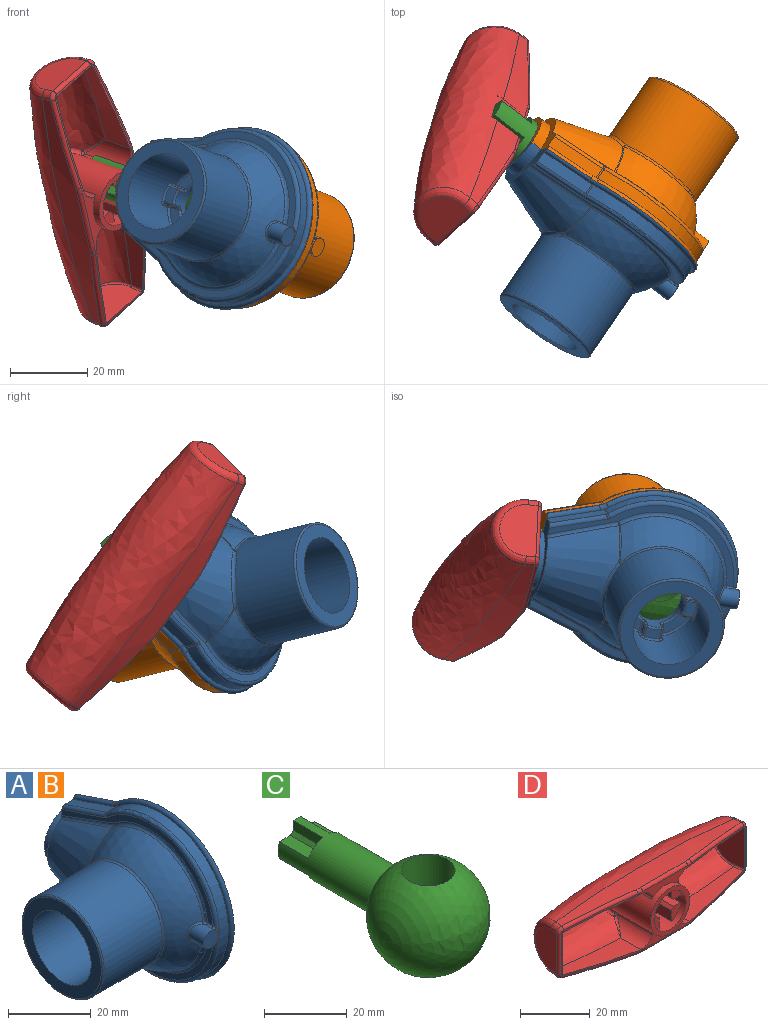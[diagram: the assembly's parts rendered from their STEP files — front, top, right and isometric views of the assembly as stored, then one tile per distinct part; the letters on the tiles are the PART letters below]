
ASSEMBLY  parts=4 mates=3
PART A: 151 faces, bbox 35.9x59.5x52.1 mm
  f0: plane 1.96x1.09mm, normal (-1,0,0), area 0.1mm2, adj f1,f148,f149,f150
  f1: cylinder r=1mm len=3mm, axis (1,0,0), area 1.2mm2, adj f0,f2,f148,f150
  f2: torus R=2mm, axis (1,0,0), area 0.9mm2, adj f1,f3,f146,f147
  f3: torus R=22mm, axis (1,0,0), area 158.3mm2, adj f2,f4,f142,f143,f144,f145,f147,f148
  f4: torus R=2mm, axis (1,0,0), area 0.9mm2, adj f3,f5,f141,f145
  f5: cylinder r=1mm len=3mm, axis (1,0,0), area 1.2mm2, adj f4,f6,f140,f148
  f6: plane 1.96x1.09mm, normal (-1,0,0), area 0.1mm2, adj f5,f7,f140,f148
  f7: torus R=6mm, axis (1,0,0), area 3.2mm2, adj f6,f8,f138,f139
  f8: plane 57x48mm, normal (1,0,0), area 1146.2mm2, adj f7,f9,f133,f134,f135,f136,f137,f138
  f9: sphere r=15mm, area 1204.3mm2, adj f8,f10,f133
  f10: cylinder r=6.5mm len=13mm, axis (-1,0,0), area 127.8mm2, adj f9,f11,f110,f111,f112,f113,f114,f115
  f11: cylinder r=0.5mm len=2mm, axis (-1,0,0), area 1.9mm2, adj f10,f12,f109,f132
  f12: sphere r=0.5mm, area 0.5mm2, adj f11,f13,f110
  f13: cylinder r=0.5mm len=2.58mm, axis (0,0,-1), area 1.9mm2, adj f12,f14,f108,f109
  f14: plane 4x2.79mm, normal (-1,0,0), area 10.1mm2, adj f13,f15,f107,f110
  f15: cylinder r=0.5mm len=2.58mm, axis (0,0,1), area 1.9mm2, adj f14,f16,f17,f106
  f16: sphere r=0.5mm, area 0.5mm2, adj f15,f110,f111
  f17: plane 2.31x2mm, normal (0,1,0), area 4.6mm2, adj f15,f18,f105,f111
  f18: cylinder r=0.5mm len=2.69mm, axis (0,0,-1), area 2mm2, adj f17,f19,f104,f112
  f19: sphere r=0.5mm, area 0.5mm2, adj f18,f20,f105
  f20: torus R=9.5mm, axis (-1,0,0), area 7.2mm2, adj f19,f21,f103,f104
  f21: cylinder r=10mm len=20mm, axis (-1,0,0), area 1089.6mm2, adj f20,f22,f61,f85,f86,f87,f88,f89
  f22: cylinder r=0.5mm len=2mm, axis (-1,0,0), area 1.9mm2, adj f21,f23,f102,f103
  f23: plane 2.31x2mm, normal (0,0,1), area 4.6mm2, adj f22,f24,f60,f115
  f24: cylinder r=0.5mm len=2.58mm, axis (0,-1,0), area 1.9mm2, adj f23,f25,f26,f102
  f25: sphere r=0.5mm, area 0.3mm2, adj f24,f115,f116
  f26: plane 4x2.79mm, normal (-1,0,0), area 10.1mm2, adj f24,f27,f101,f116
  f27: cylinder r=0.5mm len=2.58mm, axis (0,1,0), area 1.9mm2, adj f26,f28,f29,f100
  f28: sphere r=0.5mm, area 0.4mm2, adj f27,f116,f117
  f29: plane 2.31x2mm, normal (0,0,-1), area 4.6mm2, adj f27,f30,f99,f117
  f30: cylinder r=0.5mm len=2.69mm, axis (0,-1,0), area 2mm2, adj f29,f31,f32,f118
  f31: sphere r=0.5mm, area 0.7mm2, adj f30,f98,f99
  f32: plane 6.01x6.01mm, normal (-1,0,0), area 17mm2, adj f30,f33,f98,f119
  f33: cylinder r=0.5mm len=2.69mm, axis (0,0,-1), area 2mm2, adj f32,f34,f35,f120
  f34: sphere r=0.5mm, area 0.5mm2, adj f33,f97,f98
  f35: plane 2.31x2mm, normal (0,1,0), area 4.6mm2, adj f33,f36,f97,f121
  f36: cylinder r=0.5mm len=2.58mm, axis (0,0,1), area 1.9mm2, adj f35,f37,f38,f96
  f37: sphere r=0.5mm, area 0.5mm2, adj f36,f121,f122
  f38: plane 4x2.79mm, normal (-1,0,0), area 10.1mm2, adj f36,f39,f95,f122
  f39: cylinder r=0.5mm len=2.58mm, axis (0,0,-1), area 1.9mm2, adj f38,f40,f41,f94
  f40: sphere r=0.5mm, area 0.5mm2, adj f39,f122,f123
  f41: plane 2.31x2mm, normal (0,-1,0), area 4.6mm2, adj f39,f42,f93,f123
  f42: cylinder r=0.5mm len=2.69mm, axis (0,0,1), area 2mm2, adj f41,f43,f44,f124
  f43: sphere r=0.5mm, area 0.5mm2, adj f42,f92,f93
  f44: plane 6.01x6.01mm, normal (-1,0,0), area 17mm2, adj f42,f45,f92,f125
  f45: cylinder r=0.5mm len=2.69mm, axis (0,-1,0), area 2mm2, adj f44,f46,f47,f126
  f46: sphere r=0.5mm, area 0.6mm2, adj f45,f91,f92
  f47: plane 2.31x2mm, normal (0,0,-1), area 4.6mm2, adj f45,f48,f91,f127
  f48: cylinder r=0.5mm len=2.58mm, axis (0,1,0), area 1.9mm2, adj f47,f49,f50,f90
  f49: sphere r=0.5mm, area 0.8mm2, adj f48,f127,f128
  f50: plane 4x2.79mm, normal (-1,0,0), area 10.1mm2, adj f48,f51,f89,f128
  f51: cylinder r=0.5mm len=2.58mm, axis (0,-1,0), area 1.9mm2, adj f50,f52,f53,f54,f88
  f52: sphere r=0.5mm, area 0mm2, adj f51,f129
  f53: sphere r=0.5mm, area 0.2mm2, adj f51,f128,f129
  f54: plane 2.31x2mm, normal (0,0,1), area 4.6mm2, adj f51,f55,f87,f129
  f55: cylinder r=0.5mm len=2.69mm, axis (0,1,0), area 2mm2, adj f54,f56,f57,f130
  f56: sphere r=0.5mm, area 0.6mm2, adj f55,f86,f87
  f57: plane 6.01x6.01mm, normal (-1,0,0), area 17mm2, adj f55,f58,f86,f131
  f58: cylinder r=0.5mm len=2.69mm, axis (0,0,1), area 2mm2, adj f57,f59,f109,f132
  f59: sphere r=0.5mm, area 0.5mm2, adj f58,f85,f86
  f60: cylinder r=0.5mm len=2.69mm, axis (0,1,0), area 2mm2, adj f23,f103,f104,f114
  f61: plane 27x27mm, normal (-1,0,0), area 258.4mm2, adj f21,f62
  f62: torus R=13.5mm, axis (1,0,0), area 68.2mm2, adj f61,f63
  f63: cylinder r=14mm len=28mm, axis (1,0,0), area 1742mm2, adj f62,f64,f84
  f64: bspline ~17.52x3.73mm, area 19.6mm2, adj f63,f65,f82,f83
  f65: sphere r=1mm, area 0.1mm2, adj f64,f66,f84
  f66: torus R=16.9mm, axis (0,-1,0), area 3.5mm2, adj f65,f67,f81,f82
  f67: sphere r=1mm, area 0.1mm2, adj f66,f68,f69
  f68: bspline ~23.13x9.23mm, area 21.5mm2, adj f67,f82,f136,f145
  f69: torus R=20.12mm, axis (1,0,0), area 52.7mm2, adj f67,f70,f81,f145
  f70: bspline ~1.33x1.14mm, area 1mm2, adj f69,f71,f72,f79
  f71: cylinder r=0.5mm len=1.89mm, axis (0,1,0), area 2mm2, adj f70,f79,f144,f145
  f72: bspline ~5.86x4.64mm, area 6.9mm2, adj f70,f73,f79,f81
  f73: bspline ~1.33x1.14mm, area 1mm2, adj f72,f74,f75,f79
  f74: cylinder r=0.5mm len=1.89mm, axis (0,1,0), area 2mm2, adj f73,f79,f142,f147
  f75: torus R=20.12mm, axis (1,0,0), area 52.7mm2, adj f73,f76,f81,f147
  f76: sphere r=1mm, area 0.2mm2, adj f75,f77,f78
  f77: torus R=16.9mm, axis (0,-1,0), area 3.5mm2, adj f76,f81,f82,f83
  f78: bspline ~25.11x10.02mm, area 21.5mm2, adj f76,f82,f136,f147
  f79: cylinder r=2.5mm len=5.1mm, axis (0,1,0), area 46.9mm2, adj f70,f71,f72,f73,f74,f80,f142,f144
  f80: plane 5.14x5.14mm, normal (0,-1,0), area 19.6mm2, adj f79,f143
  f81: sphere r=20mm, area 755.1mm2, adj f66,f69,f72,f75,f77,f84
  f82: cone r=10mm half-angle=18.4deg, axis (0,-1,0), area 540.7mm2, adj f64,f66,f68,f77,f78,f136
  f83: sphere r=1mm, area 0.1mm2, adj f64,f77,f84
  f84: torus R=15mm, axis (1,0,0), area 55.8mm2, adj f63,f65,f81,f83
  f85: cylinder r=0.5mm len=2mm, axis (-1,0,0), area 1.9mm2, adj f21,f59,f108,f109
  f86: torus R=9.5mm, axis (-1,0,0), area 7.2mm2, adj f21,f56,f57,f59
  f87: cylinder r=0.5mm len=2mm, axis (-1,0,0), area 1.9mm2, adj f21,f54,f56,f88
  f88: bspline ~1.23x1.21mm, area 1mm2, adj f21,f51,f87,f89
  f89: torus R=9.5mm, axis (-1,0,0), area 3.3mm2, adj f21,f50,f88,f90
  f90: bspline ~1.29x1.2mm, area 1mm2, adj f21,f48,f89,f91
  f91: cylinder r=0.5mm len=2mm, axis (-1,0,0), area 1.9mm2, adj f21,f46,f47,f90
  f92: torus R=9.5mm, axis (-1,0,0), area 7.2mm2, adj f21,f43,f44,f46
  f93: cylinder r=0.5mm len=2mm, axis (-1,0,0), area 1.9mm2, adj f21,f41,f43,f94
  f94: bspline ~1.23x1.21mm, area 1mm2, adj f21,f39,f93,f95
  f95: torus R=9.5mm, axis (-1,0,0), area 3.3mm2, adj f21,f38,f94,f96
  f96: bspline ~1.29x1.2mm, area 1mm2, adj f21,f36,f95,f97
  f97: cylinder r=0.5mm len=2mm, axis (-1,0,0), area 1.9mm2, adj f21,f34,f35,f96
  f98: torus R=9.5mm, axis (-1,0,0), area 7.2mm2, adj f21,f31,f32,f34
  f99: cylinder r=0.5mm len=2mm, axis (-1,0,0), area 1.9mm2, adj f21,f29,f31,f100
  f100: bspline ~1.23x1.21mm, area 1mm2, adj f21,f27,f99,f101
  f101: torus R=9.5mm, axis (-1,0,0), area 3.3mm2, adj f21,f26,f100,f102
  f102: bspline ~1.29x1.2mm, area 1mm2, adj f21,f22,f24,f101
  f103: sphere r=0.5mm, area 0.3mm2, adj f20,f22,f60
  f104: plane 6.01x6.01mm, normal (-1,0,0), area 17mm2, adj f18,f20,f60,f113
  f105: cylinder r=0.5mm len=2mm, axis (-1,0,0), area 1.9mm2, adj f17,f19,f21,f106
  f106: bspline ~1.23x1.21mm, area 1mm2, adj f15,f21,f105,f107
  f107: torus R=9.5mm, axis (-1,0,0), area 3.3mm2, adj f14,f21,f106,f108
  f108: bspline ~1.29x1.2mm, area 1mm2, adj f13,f21,f85,f107
  f109: plane 2.31x2mm, normal (0,-1,0), area 4.6mm2, adj f11,f13,f58,f85
  f110: torus R=7mm, axis (-1,0,0), area 3mm2, adj f10,f12,f14,f16
  f111: cylinder r=0.5mm len=2mm, axis (-1,0,0), area 1.9mm2, adj f10,f16,f17,f112
  f112: bspline ~1.22x1.2mm, area 0.9mm2, adj f10,f18,f111,f113
  f113: torus R=7mm, axis (-1,0,0), area 3.6mm2, adj f10,f104,f112,f114
  f114: bspline ~1.27x1.21mm, area 0.9mm2, adj f10,f60,f113,f115
  f115: cylinder r=0.5mm len=2mm, axis (-1,0,0), area 1.9mm2, adj f10,f23,f25,f114
  f116: torus R=7mm, axis (-1,0,0), area 3mm2, adj f10,f25,f26,f28
  f117: cylinder r=0.5mm len=2mm, axis (-1,0,0), area 1.9mm2, adj f10,f28,f29,f118
  f118: bspline ~1.22x1.2mm, area 0.9mm2, adj f10,f30,f117,f119
  f119: torus R=7mm, axis (-1,0,0), area 3.6mm2, adj f10,f32,f118,f120
  f120: bspline ~1.27x1.21mm, area 0.9mm2, adj f10,f33,f119,f121
  f121: cylinder r=0.5mm len=2mm, axis (-1,0,0), area 1.9mm2, adj f10,f35,f37,f120
  f122: torus R=7mm, axis (-1,0,0), area 3mm2, adj f10,f37,f38,f40
  f123: cylinder r=0.5mm len=2mm, axis (-1,0,0), area 1.9mm2, adj f10,f40,f41,f124
  f124: bspline ~1.22x1.2mm, area 0.9mm2, adj f10,f42,f123,f125
  f125: torus R=7mm, axis (-1,0,0), area 3.6mm2, adj f10,f44,f124,f126
  f126: bspline ~1.27x1.21mm, area 0.9mm2, adj f10,f45,f125,f127
  f127: cylinder r=0.5mm len=2mm, axis (-1,0,0), area 1.9mm2, adj f10,f47,f49,f126
  f128: torus R=7mm, axis (-1,0,0), area 3mm2, adj f10,f49,f50,f53
  f129: cylinder r=0.5mm len=2mm, axis (-1,0,0), area 1.9mm2, adj f10,f52,f53,f54,f130
  f130: bspline ~1.22x1.2mm, area 0.9mm2, adj f10,f55,f129,f131
  f131: torus R=7mm, axis (-1,0,0), area 3.6mm2, adj f10,f57,f130,f132
  f132: bspline ~1.27x1.21mm, area 0.9mm2, adj f10,f11,f58,f131
  f133: cylinder r=6.5mm len=19.48mm, axis (0,1,0), area 397.8mm2, adj f8,f9,f134
  f134: plane 16x8mm, normal (0,1,0), area 34.2mm2, adj f8,f133,f137
  f135: cylinder r=1mm len=13.58mm, axis (0,-0.95,-0.32), area 21.7mm2, adj f8,f136,f149,f150
  f136: plane 26.46x10.14mm, normal (0,1,0), area 83.3mm2, adj f8,f68,f78,f82,f135,f137,f139,f140
  f137: cylinder r=8mm len=16mm, axis (0,-1,0), area 75.4mm2, adj f8,f134,f136
  f138: torus R=23mm, axis (1,0,0), area 168.5mm2, adj f7,f8,f148,f149
  f139: cylinder r=1mm len=13.58mm, axis (0,0.95,-0.32), area 21.7mm2, adj f7,f8,f136,f140
  f140: plane 14.21x4.74mm, normal (0,0.32,0.95), area 44.9mm2, adj f5,f6,f136,f139,f141
  f141: cylinder r=1mm len=14.84mm, axis (0,0.95,-0.32), area 23.8mm2, adj f4,f136,f140,f145
  f142: bspline ~1.53x1.14mm, area 1mm2, adj f3,f74,f79,f143
  f143: bspline ~4.54x1.2mm, area 2.1mm2, adj f3,f80,f142,f144
  f144: bspline ~1.52x1.14mm, area 1mm2, adj f3,f71,f79,f143
  f145: plane 51.85x19.4mm, normal (-1,0,0), area 108.1mm2, adj f3,f4,f68,f69,f71,f136,f141
  f146: cylinder r=1mm len=14.84mm, axis (0,-0.95,-0.32), area 23.8mm2, adj f2,f136,f147,f150
  f147: plane 51.85x19.4mm, normal (-1,0,0), area 108.1mm2, adj f2,f3,f74,f75,f78,f136,f146
  f148: cylinder r=23mm len=46mm, axis (1,0,0), area 318.3mm2, adj f0,f1,f3,f5,f6,f138
  f149: torus R=6mm, axis (1,0,0), area 3.2mm2, adj f0,f8,f135,f138
  f150: plane 14.21x4.74mm, normal (0,0.32,-0.95), area 44.9mm2, adj f0,f1,f135,f136,f146
PART B: same geometry as A
PART C: 20 faces, bbox 30x60x30 mm
  f0: sphere r=15mm, area 2408.6mm2, adj f1,f19
  f1: cylinder r=6.5mm len=31.48mm, axis (0,-1,0), area 1030.3mm2, adj f0,f2,f3,f4,f5,f6,f7,f8
  f2: plane 13x13mm, normal (0,1,0), area 85.2mm2, adj f1,f3,f4,f6,f7,f9,f10,f12
  f3: plane 10x2.88mm, normal (-1,0,0), area 28.8mm2, adj f1,f2,f5,f15
  f4: plane 10x3.75mm, normal (0,0,-1), area 37.5mm2, adj f1,f2,f5,f15
  f5: plane 4.75x3.88mm, normal (0,1,0), area 11.9mm2, adj f1,f3,f4,f15
  f6: plane 10x2.88mm, normal (1,0,0), area 28.8mm2, adj f1,f2,f8,f17
  f7: plane 10x3.75mm, normal (0,0,1), area 37.5mm2, adj f1,f2,f8,f17
  f8: plane 4.75x3.88mm, normal (0,1,0), area 11.9mm2, adj f1,f6,f7,f17
  f9: plane 10x3.75mm, normal (0,0,-1), area 37.5mm2, adj f1,f2,f11,f16
  f10: plane 10x2.88mm, normal (1,0,0), area 28.8mm2, adj f1,f2,f11,f16
  f11: plane 4.75x3.88mm, normal (0,1,0), area 11.9mm2, adj f1,f9,f10,f16
  f12: plane 10x3.75mm, normal (0,0,1), area 37.5mm2, adj f1,f2,f14,f18
  f13: plane 10x2.88mm, normal (-1,0,0), area 28.8mm2, adj f1,f2,f14,f18
  f14: plane 4.75x3.88mm, normal (0,1,0), area 11.9mm2, adj f1,f12,f13,f18
  f15: plane 10x1mm, normal (-0.71,0,-0.71), area 14.1mm2, adj f2,f3,f4,f5
  f16: plane 10x1mm, normal (0.71,0,-0.71), area 14.1mm2, adj f2,f9,f10,f11
  f17: plane 10x1mm, normal (0.71,0,0.71), area 14.1mm2, adj f2,f6,f7,f8
  f18: plane 10x1mm, normal (-0.71,0,0.71), area 14.1mm2, adj f2,f12,f13,f14
  f19: cylinder r=6.5mm len=27.04mm, axis (0,0,1), area 1104.2mm2, adj f0
PART D: 87 faces, bbox 87.2x36.2x26 mm
  f0: offset ~58.37x11.25mm, area 157.5mm2, adj f1,f17,f38,f41,f56
  f1: offset ~58.37x25.96mm, area 823mm2, adj f0,f33,f39,f80,f83,f84
  f2: offset ~58.37x11.25mm, area 157.5mm2, adj f16,f34,f37,f43,f54
  f3: plane 10x3.75mm, normal (1,0,0), area 37.5mm2, adj f12,f47,f48,f51
  f4: plane 10x2.88mm, normal (0,0,1), area 28.8mm2, adj f12,f47,f48,f51
  f5: plane 10x2.88mm, normal (0,0,-1), area 28.8mm2, adj f11,f47,f48,f52
  f6: plane 10x3.75mm, normal (1,0,0), area 37.5mm2, adj f11,f47,f48,f52
  f7: plane 10x3.75mm, normal (-1,0,0), area 37.5mm2, adj f14,f47,f48,f49
  f8: plane 10x2.88mm, normal (0,0,-1), area 28.8mm2, adj f14,f47,f48,f49
  f9: plane 10x2.88mm, normal (0,0,1), area 28.8mm2, adj f13,f47,f48,f50
  f10: plane 10x3.75mm, normal (-1,0,0), area 37.5mm2, adj f13,f47,f48,f50
  f11: plane 10x1mm, normal (0.71,0,-0.71), area 14.1mm2, adj f5,f6,f48,f52
  f12: plane 10x1mm, normal (0.71,0,0.71), area 14.1mm2, adj f3,f4,f48,f51
  f13: plane 10x1mm, normal (-0.71,0,0.71), area 14.1mm2, adj f9,f10,f48,f50
  f14: plane 10x1mm, normal (-0.71,0,-0.71), area 14.1mm2, adj f7,f8,f48,f49
  f15: plane 18.26x4.47mm, normal (0,-1,0), area 41.5mm2, adj f41,f42,f45,f53,f56,f60,f74,f86
  f16: plane 26.68x20.57mm, normal (-0.17,-0.98,0), area 35.9mm2, adj f2,f30,f32,f35,f37,f42,f43,f64
  f17: plane 26.68x20.57mm, normal (0.17,-0.98,0), area 35.9mm2, adj f0,f31,f33,f38,f40,f41,f44,f57
  f18: plane 14.2x9.76mm, normal (-0.99,0.12,0), area 117.6mm2, adj f24,f25,f26,f68
  f19: plane 14.21x9.76mm, normal (0.99,0.12,0), area 117.6mm2, adj f27,f28,f29,f61
  f20: plane 18.26x4.47mm, normal (0,-1,0), area 41.5mm2, adj f43,f44,f45,f54,f55,f69,f75,f81
  f21: bspline ~78x8.25mm, area 405.4mm2, adj f23,f24,f27,f57,f58,f60,f62,f64
  f22: bspline ~78x8.25mm, area 405.4mm2, adj f23,f26,f29,f65,f67,f69,f71,f72
  f23: bspline ~78x22.96mm, area 2425.3mm2, adj f21,f22,f25,f28
  f24: bspline ~6.43x2.51mm, area 7.5mm2, adj f18,f21,f25,f66
  f25: bspline ~18.17x9.35mm, area 72.4mm2, adj f18,f23,f24,f26
  f26: bspline ~6.43x2.51mm, area 7.5mm2, adj f18,f22,f25,f70
  f27: bspline ~6.43x2.51mm, area 7.5mm2, adj f19,f21,f28,f59
  f28: bspline ~18.18x9.49mm, area 72.4mm2, adj f19,f23,f27,f29
  f29: bspline ~6.43x2.51mm, area 7.5mm2, adj f19,f22,f28,f63
  f30: plane 14.21x10.78mm, normal (0.99,-0.12,0), area 132.1mm2, adj f16,f35,f36,f37
  f31: plane 14.21x10.78mm, normal (-0.99,-0.12,0), area 132.1mm2, adj f17,f38,f39,f40
  f32: offset ~58.37x11.25mm, area 157.5mm2, adj f16,f34,f35,f42,f53
  f33: offset ~58.37x11.25mm, area 157.5mm2, adj f1,f17,f40,f44,f55
  f34: offset ~58.37x25.96mm, area 823mm2, adj f2,f32,f36,f73,f76,f79
  f35: bspline ~6.94x1.28mm, area 2.6mm2, adj f16,f30,f32,f36
  f36: bspline ~15.2x8.28mm, area 16.2mm2, adj f30,f34,f35,f37
  f37: bspline ~6.94x1.28mm, area 2.6mm2, adj f2,f16,f30,f36
  f38: bspline ~6.94x1.28mm, area 2.6mm2, adj f0,f17,f31,f39
  f39: bspline ~15.2x8.84mm, area 16.2mm2, adj f1,f31,f38,f40
  f40: bspline ~6.94x1.28mm, area 2.6mm2, adj f17,f31,f33,f39
  f41: cylinder r=10mm len=1.74mm, axis (0,0,-1), area 0.9mm2, adj f0,f15,f17,f56,f58
  f42: cylinder r=10mm len=1.74mm, axis (0,0,-1), area 0.9mm2, adj f15,f16,f32,f53,f62
  f43: cylinder r=10mm len=1.74mm, axis (0,0,-1), area 0.9mm2, adj f2,f16,f20,f54,f71
  f44: cylinder r=10mm len=1.74mm, axis (0,0,-1), area 0.9mm2, adj f17,f20,f33,f55,f67
  f45: cylinder r=8mm len=19.02mm, axis (0,-1,0), area 517.3mm2, adj f15,f20,f46,f74,f75,f79,f81,f84
  f46: plane 16x16mm, normal (0,-1,0), area 68.3mm2, adj f45,f47
  f47: cylinder r=6.5mm len=13mm, axis (0,-1,0), area 234.6mm2, adj f3,f4,f5,f6,f7,f8,f9,f10
  f48: plane 13x13mm, normal (0,-1,0), area 85.2mm2, adj f3,f4,f5,f6,f7,f8,f9,f10
  f49: plane 4.75x3.88mm, normal (0,-1,0), area 11.9mm2, adj f7,f8,f14,f47
  f50: plane 4.75x3.88mm, normal (0,-1,0), area 11.9mm2, adj f9,f10,f13,f47
  f51: plane 4.75x3.88mm, normal (0,-1,0), area 11.9mm2, adj f3,f4,f12,f47
  f52: plane 4.75x3.88mm, normal (0,-1,0), area 11.9mm2, adj f5,f6,f11,f47
  f53: cylinder r=5mm len=14.11mm, axis (0,1,0), area 63mm2, adj f15,f32,f42,f73,f74
  f54: cylinder r=5mm len=14.11mm, axis (0,-1,0), area 63mm2, adj f2,f20,f43,f75,f76
  f55: cylinder r=5mm len=14.11mm, axis (0,-1,0), area 63mm2, adj f20,f33,f44,f80,f81
  f56: cylinder r=5mm len=14.11mm, axis (0,1,0), area 63mm2, adj f0,f15,f41,f83,f86
  f57: bspline ~36.87x7.44mm, area 40.9mm2, adj f17,f21,f58,f59
  f58: bspline ~6.15x1.7mm, area 2.6mm2, adj f21,f41,f57,f60
  f59: bspline ~2.3x2.12mm, area 3.6mm2, adj f17,f27,f57,f61
  f60: bspline ~29.42x1.18mm, area 28.7mm2, adj f15,f21,f58,f62
  f61: cylinder r=1mm len=14.13mm, axis (0,0,-1), area 21.4mm2, adj f17,f19,f59,f63
  f62: bspline ~6.15x1.7mm, area 2.6mm2, adj f21,f42,f60,f64
  f63: bspline ~2.44x1.97mm, area 3.6mm2, adj f17,f29,f61,f65
  f64: bspline ~36.87x7.44mm, area 40.9mm2, adj f16,f21,f62,f66
  f65: bspline ~36.87x7.44mm, area 40.9mm2, adj f17,f22,f63,f67
  f66: bspline ~2.44x1.97mm, area 3.6mm2, adj f16,f24,f64,f68
  f67: bspline ~6.15x1.7mm, area 2.6mm2, adj f22,f44,f65,f69
  f68: cylinder r=1mm len=14.13mm, axis (0,0,-1), area 21.4mm2, adj f16,f18,f66,f70
  f69: bspline ~29.42x1.18mm, area 28.7mm2, adj f20,f22,f67,f71
  f70: bspline ~2.3x2.12mm, area 3.6mm2, adj f16,f26,f68,f72
  f71: bspline ~6.15x1.7mm, area 2.6mm2, adj f22,f43,f69,f72
  f72: bspline ~36.87x7.44mm, area 40.9mm2, adj f16,f22,f70,f71
  f73: bspline ~7.12x4.83mm, area 3.4mm2, adj f34,f53,f77
  f74: cylinder r=1mm len=14.11mm, axis (0,-1,0), area 18mm2, adj f15,f45,f53,f77
  f75: cylinder r=1mm len=14.11mm, axis (0,-1,0), area 18mm2, adj f20,f45,f54,f78
  f76: bspline ~6.73x4.66mm, area 3.4mm2, adj f34,f54,f78
  f77: sphere r=1mm, area 1.1mm2, adj f73,f74,f79
  f78: sphere r=1mm, area 1.1mm2, adj f75,f76,f79
  f79: bspline ~15.92x5.38mm, area 28.8mm2, adj f34,f45,f77,f78
  f80: bspline ~7.12x4.83mm, area 3.4mm2, adj f1,f55,f82
  f81: cylinder r=1mm len=14.11mm, axis (0,-1,0), area 18mm2, adj f20,f45,f55,f82
  f82: sphere r=1mm, area 0.9mm2, adj f80,f81,f84
  f83: bspline ~6.73x4.66mm, area 3.4mm2, adj f1,f56,f85
  f84: bspline ~15.09x4.63mm, area 28.8mm2, adj f1,f45,f82,f85
  f85: sphere r=1mm, area 0.9mm2, adj f83,f84,f86
  f86: cylinder r=1mm len=14.11mm, axis (0,-1,0), area 18mm2, adj f15,f45,f56,f85
PLACE A rot(axis=(0.15,0.32,0.94),57.2deg) t=(37.54,-11.21,59.52)mm
PLACE B rot(axis=(0.45,-0.89,-0.07),162.6deg) t=(37.54,-11.21,59.52)mm
PLACE C rot(axis=(0.53,-0.62,0.58),70.6deg) t=(37.54,-11.21,59.52)mm
PLACE D rot(axis=(0.5,-0.86,0.11),124.7deg) t=(6,5.06,64.51)mm
MATE revolute C.f1 <-> B.f133  axis (0.76,-0.59,-0.26) through (27.2,-3.26,63.08)mm
MATE revolute C.f1 <-> A.f133  axis (0.76,-0.59,-0.26) through (27.2,-3.26,63.08)mm
MATE pin_slot C.f1 <-> D.f45  axis (-0.76,0.59,0.26) through (3.12,15.24,71.39)mm
